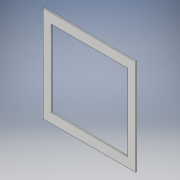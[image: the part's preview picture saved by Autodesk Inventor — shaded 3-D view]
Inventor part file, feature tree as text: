
AUTODESK INVENTOR PART (.ipt)
format: ipt  version: 2017 (Build 210142000, 142)  size: 107,520 bytes
history: native  units: in
note: dims shown in document units (in); Inventor stores cm internally (conversion verified against a paired STEP export)
features: extrude x2, sketch x2
ambient origin geometry x8: Origin, YZ Plane, XZ Plane, XY Plane, X Axis, Y Axis, Z Axis, Center Point
bodies: Solid1 (feature_tree)
feature tree (4):
  extrude  "Extrusion1"  Depth=20.0in
  extrude  "Extrusion2"  Depth=16.0in
  sketch  "Sketch1"  dims[d0=19.333in d1=20.0in]
  sketch  "Sketch2"  dims[d2=0.25in d3=0.0in d4=16.0in d5=16.0in d6=0.25in d7=0.0in]
